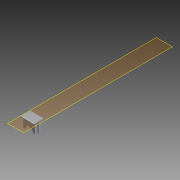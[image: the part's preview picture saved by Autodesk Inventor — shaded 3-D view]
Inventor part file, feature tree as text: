
AUTODESK INVENTOR PART (.ipt)
format: ipt  version: 2012 (Build 160160000, 160)  size: 244,224 bytes
history: native  units: in
note: dims shown in document units (in); Inventor stores cm internally (conversion verified against a paired STEP export)
features: sketch x7, extrude x7, reference x5, projected_geometry x5, fillet x3, plane x2
ambient origin geometry x8: Origin, YZ Plane, XZ Plane, XY Plane, X Axis, Y Axis, Z Axis, Center Point
feature tree (29):
  plane  "Work Plane8"
  sketch  "Sketch21"  dims[d99=0.0118in d100=0.0118in]
  plane  "Work Plane9"
  extrude  "Extrusion20"  Depth=0.0118in
  extrude  "Extrusion21"  Depth=0.0118in
  extrude  "Extrusion22"  Depth=0.0118in
  extrude  "Extrusion23"  Depth=0.0118in
  sketch  "Sketch25"  dims[d108=0.0118in d109=0.0118in d110=0.0118in d111=0.3937in d112=0.0in]
  fillet  "Fillet13"  Radius=0.0118in
  extrude  "Extrusion24"  Depth=0.0118in
  fillet  "Fillet14"  Radius=0.0118in
  fillet  "Fillet15"  Radius=0.3937in
  extrude  "Extrusion25"  Depth=0.0984in
  extrude  "Extrusion26"  Depth=0.0118in
  reference  "Reference41"
  sketch  "Sketch22"  dims[d101=0.0118in d102=0.0118in]
  reference  "Reference42"
  sketch  "Sketch23"  dims[d103=0.0118in d104=0.0118in]
  projected_geometry  "Projected Loop8"
  reference  "Reference43"
  reference  "Reference44"
  sketch  "Sketch24"  dims[d105=0.0118in d106=0.0118in d107=0.0118in]
  projected_geometry  "Projected Loop9"
  reference  "Reference45"
  sketch  "Sketch26"  dims[d113=0.3937in d114=0.0in d115=0.0984in]
  projected_geometry  "Projected Loop10"
  projected_geometry  "Projected Loop11"
  sketch  "Sketch27"  dims[d116=0.0984in d117=0.0118in d118=0.0118in d119=0.0591in d120=0.0in d121=0.8016in d122=0.2672in d123=0.2672in d124=0.0295in d125=0.0591in d126=0.0591in d127=0.0in d128=0.0787in d129=0.0591in d130=0.0in d131=0.0787in d132=0.0394in d133=0.0059in d134=0.0in d135=0.0059in d136=0.0in]
  projected_geometry  "Projected Loop12"
